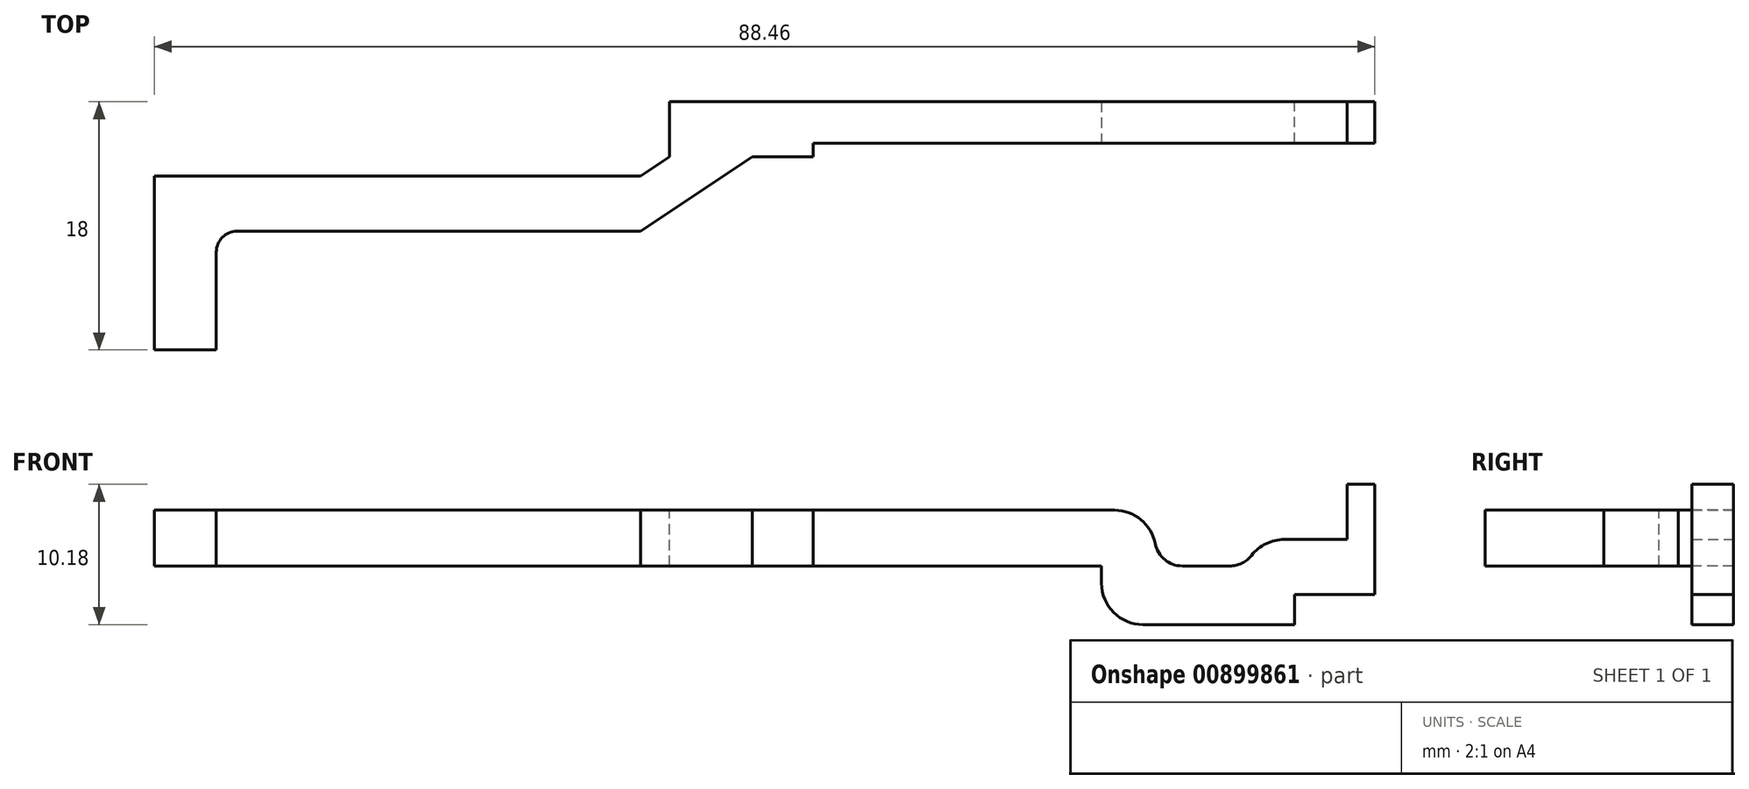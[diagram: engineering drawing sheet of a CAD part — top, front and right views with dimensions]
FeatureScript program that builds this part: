
annotation { "Feature Type Name" : "Feature", "Feature Type Description" : "" }
export const myFeature = defineFeature(function(context is Context, id is Id, definition is map)
    precondition{}
    {
        {
            var Q0;
            Q0=qCreatedBy(makeId("Top.planeOp"),FACE);
            var sketch = newSketch(context, id + "F0", { "sketchPlane" : qUnion([Q0])});
            skLineSegment(sketch, "E0.bottom", {"start": v(0, 0) * mm, "end": v(4.5, 0) * mm});
            skLineSegment(sketch, "E0.top", {"start": v(0, 8.6) * mm, "end": v(4.5, 8.6) * mm});
            skLineSegment(sketch, "E0.left", {"start": v(0, 0) * mm, "end": v(0, 8.6) * mm});
            skLineSegment(sketch, "E0.right", {"start": v(4.5, 0) * mm, "end": v(4.5, 8.6) * mm});
            skLineSegment(sketch, "E1.bottom", {"start": v(0, 8.6) * mm, "end": v(35.25, 8.6) * mm});
            skLineSegment(sketch, "E1.top", {"start": v(0, 12.6) * mm, "end": v(35.25, 12.6) * mm});
            skLineSegment(sketch, "E1.left", {"start": v(0, 8.6) * mm, "end": v(0, 12.6) * mm});
            skLineSegment(sketch, "E1.right", {"start": v(35.25, 8.6) * mm, "end": v(35.25, 12.6) * mm});
            skLineSegment(sketch, "E2.bottom", {"start": v(37.35, 18) * mm, "end": v(47.76, 18) * mm});
            skLineSegment(sketch, "E2.top", {"start": v(37.35, 14) * mm, "end": v(47.76, 14) * mm});
            skLineSegment(sketch, "E2.left", {"start": v(37.35, 18) * mm, "end": v(37.35, 14) * mm});
            skLineSegment(sketch, "E2.right", {"start": v(47.76, 18) * mm, "end": v(47.76, 14) * mm});
            skLineSegment(sketch, "E3", {"start": v(35.25, 12.6) * mm, "end": v(37.35, 14) * mm});
            skLineSegment(sketch, "E4", {"start": v(35.25, 8.6) * mm, "end": v(43.35, 14) * mm});
            skLineSegment(sketch, "E5.bottom", {"start": v(47.76, 18) * mm, "end": v(68.66, 18) * mm});
            skLineSegment(sketch, "E5.top", {"start": v(47.76, 15) * mm, "end": v(68.66, 15) * mm});
            skLineSegment(sketch, "E5.left", {"start": v(47.76, 18) * mm, "end": v(47.76, 15) * mm});
            skLineSegment(sketch, "E5.right", {"start": v(68.66, 18) * mm, "end": v(68.66, 15) * mm});
            skLineSegment(sketch, "E6.bottom", {"start": v(68.66, 18) * mm, "end": v(88.46, 18) * mm});
            skLineSegment(sketch, "E6.top", {"start": v(68.66, 15) * mm, "end": v(88.46, 15) * mm});
            skLineSegment(sketch, "E6.right", {"start": v(88.46, 18) * mm, "end": v(88.46, 15) * mm});
            skSolve(sketch);
        }
        {
            var Q0;
            Q0=makeQuery(id+"F0.imprint","IMPRINT",FACE,{"disambiguationData":[TD([[makeQuery(id+"F0.imprint","IMPRINT",EDGE,{"derivedFrom":sQuery(id+"F0.wireOp",EDGE,"E0.bottom")}),1.0]])]});
            var Q1;
            Q1=makeQuery(id+"F0.imprint","IMPRINT",FACE,{"disambiguationData":[TD([[makeQuery(id+"F0.imprint","IMPRINT",EDGE,{"derivedFrom":sQuery(id+"F0.wireOp",EDGE,"E1.top")}),-1.0]])]});
            var Q2;
            Q2=makeQuery(id+"F0.imprint","IMPRINT",FACE,{"disambiguationData":[TD([[makeQuery(id+"F0.imprint","IMPRINT",EDGE,{"derivedFrom":sQuery(id+"F0.wireOp",EDGE,"E1.right")}),-1.0]])]});
            var Q3;
            Q3=makeQuery(id+"F0.imprint","IMPRINT",FACE,{"disambiguationData":[TD([[makeQuery(id+"F0.imprint","IMPRINT",EDGE,{"derivedFrom":sQuery(id+"F0.wireOp",EDGE,"E2.bottom")}),-1.0]])]});
            var Q4;
            Q4=makeQuery(id+"F0.imprint","IMPRINT",FACE,{"disambiguationData":[TD([[makeQuery(id+"F0.imprint","IMPRINT",EDGE,{"derivedFrom":sQuery(id+"F0.wireOp",EDGE,"E5.bottom")}),-1.0]])]});
            extrude(context, id + "F1", {"entities" : qUnion([Q0, Q1, Q2, Q3, Q4]), "oppositeDirection" : true, "depth" : 4.05 * mm, "offsetDistance" : 25 * mm});
        }
        {
            var Q0;
            Q0=makeQuery(id+"F0.imprint","IMPRINT",FACE,{"disambiguationData":[TD([[makeQuery(id+"F0.imprint","IMPRINT",EDGE,{"derivedFrom":sQuery(id+"F0.wireOp",EDGE,"E6.bottom")}),-1.0]])]});
            extrude(context, id + "F2", {"entities" : qUnion([Q0]), "oppositeDirection" : true, "depth" : 8.3 * mm, "offsetDistance" : 25 * mm});
        }
        {
            var Q0;
            Q0=makeQuery(id+"F0.imprint","IMPRINT",FACE,{"disambiguationData":[TD([[makeQuery(id+"F0.imprint","IMPRINT",EDGE,{"derivedFrom":sQuery(id+"F0.wireOp",EDGE,"E6.bottom")}),-1.0]])]});
            extrude(context, id + "F3", {"entities" : qUnion([Q0]), "operationType" : NewBodyOperationType.ADD, "depth" : 1.88 * mm, "offsetDistance" : 25 * mm});
        }
        {
            var Q0;
            {var subQ0=sQuery(id+"F0.wireOp",EDGE,"E6.bottom");Q0=makeQuery(id+"F3.boolean.opBoolean","MERGE",FACE,{"derivedFrom":[makeQuery(id+"F2.opExtrude","SWEPT_FACE",FACE,{"disambiguationData":[OSD([subQ0])]}),makeQuery(id+"F3.opExtrude","SWEPT_FACE",FACE,{"disambiguationData":[OSD([subQ0])]})]});}
            var sketch = newSketch(context, id + "F4", { "sketchPlane" : qUnion([Q0])});
            skLineSegment(sketch, "E7.bottom", {"start": v(-86.46, 1.88) * mm, "end": v(-88.46, 1.88) * mm});
            skLineSegment(sketch, "E7.top", {"start": v(-86.46, -2.12) * mm, "end": v(-88.46, -2.12) * mm});
            skLineSegment(sketch, "E7.left", {"start": v(-86.46, 1.88) * mm, "end": v(-86.46, -2.12) * mm});
            skLineSegment(sketch, "E7.right", {"start": v(-88.46, 1.88) * mm, "end": v(-88.46, -2.12) * mm});
            skLineSegment(sketch, "E8.bottom", {"start": v(-88.46, -6.12) * mm, "end": v(-82.66, -6.12) * mm});
            skLineSegment(sketch, "E8.top", {"start": v(-88.46, -2.12) * mm, "end": v(-82.66, -2.12) * mm});
            skLineSegment(sketch, "E8.left", {"start": v(-88.46, -6.12) * mm, "end": v(-88.46, -2.12) * mm});
            skLineSegment(sketch, "E8.right", {"start": v(-82.66, -6.12) * mm, "end": v(-82.66, -2.12) * mm});
            skLineSegment(sketch, "E9", {"start": v(-68.66, -4.04) * mm, "end": v(-68.66, -8.3) * mm});
            skLineSegment(sketch, "E10", {"start": v(-88.46, -8.3) * mm, "end": v(-88.46, 1.88) * mm});
            skLineSegment(sketch, "E11", {"start": v(-68.66, 1.88) * mm, "end": v(-68.66, -4.04) * mm});
            skLineSegment(sketch, "E12", {"start": v(-82.66, -6.12) * mm, "end": v(-82.66, -8.3) * mm});
            skLineSegment(sketch, "E13", {"start": v(-82.66, -8.3) * mm, "end": v(-72.6, -8.3) * mm});
            skLineSegment(sketch, "E14", {"start": v(-72.6, -8.3) * mm, "end": v(-68.66, -8.3) * mm});
            skLineSegment(sketch, "E15", {"start": v(-68.66, 0) * mm, "end": v(-72.6, 0) * mm});
            skLineSegment(sketch, "E16", {"start": v(-72.6, 0) * mm, "end": v(-72.6, -4.04) * mm});
            skLineSegment(sketch, "E17", {"start": v(-72.6, -4.04) * mm, "end": v(-79.1, -4.04) * mm});
            skLineSegment(sketch, "E18", {"start": v(-79.1, -4.04) * mm, "end": v(-79.1, -2.12) * mm});
            skLineSegment(sketch, "E19", {"start": v(-79.1, -2.12) * mm, "end": v(-82.66, -2.12) * mm});
            skSolve(sketch);
        }
        {
            var Q0;
            {var subQ0=sQuery(id+"F4.wireOp",EDGE,"M4Aj1AxQ-FL5n-KYll-gw7S-FemKZirzfWIh");var subQ1=sQuery(id+"F4.wireOp",EDGE,"98212406-444c-4821-9b9e-8422945bcfc3");var subQ2=makeQuery(id+"F4.imprint","INTERSECT",VERTEX,{"disambiguationData":[OD(0.0)],"derivedFrom":[subQ1,subQ0]});Q0=makeQuery(id+"F4.imprint","IMPRINT",FACE,{"disambiguationData":[TD([[makeQuery(id+"F4.imprint","IMPRINT",EDGE,{"disambiguationData":[TD([[subQ2,-1.0]])],"derivedFrom":subQ1}),1.0]])]});}
            var Q1;
            {var subQ0=sQuery(id+"F4.wireOp",EDGE,"E8.bottom");Q1=makeQuery(id+"F4.imprint","IMPRINT",FACE,{"disambiguationData":[TD([[makeQuery(id+"F4.imprint","IMPRINT",EDGE,{"derivedFrom":subQ0}),-1.0]])]});}
            var Q2;
            {var subQ2=sQuery(id+"F4.wireOp",EDGE,"E7.left");Q2=makeQuery(id+"F4.imprint","IMPRINT",FACE,{"disambiguationData":[TD([[makeQuery(id+"F4.imprint","IMPRINT",EDGE,{"derivedFrom":subQ2}),1.0]])]});}
            extrude(context, id + "F5", {"entities" : qUnion([Q0, Q1, Q2]), "operationType" : NewBodyOperationType.REMOVE, "oppositeDirection" : true, "depth" : 25 * mm, "offsetDistance" : 25 * mm});
        }
        {
            var Q0;
            Q0=makeQuery(id+"F2.opExtrude","CAP_EDGE",EDGE,{"disambiguationData":[OSD([sQuery(id+"F0.wireOp",EDGE,"E5.right")])],"isStart":false});
            var Q1;
            Q1=makeQuery(id+"F5.boolean.opBoolean","COPY",EDGE,{"derivedFrom":makeQuery(id+"F5.opExtrude","SWEPT_EDGE",EDGE,{"disambiguationData":[OSD([sQuery(id+"F0.wireOp",EDGE,"E6.bottom"),sQuery(id+"F4.wireOp",EDGE,"E12"),sQuery(id+"F4.wireOp",EDGE,"E13")])]})});
            var Q2;
            Q2=makeQuery(id+"F5.boolean.opBoolean","COPY",EDGE,{"derivedFrom":makeQuery(id+"F5.opExtrude","SWEPT_EDGE",EDGE,{"disambiguationData":[OSD([sQuery(id+"F4.wireOp",EDGE,"E15"),sQuery(id+"F4.wireOp",EDGE,"E16")])]})});
            var Q3;
            Q3=makeQuery(id+"F5.boolean.opBoolean","COPY",EDGE,{"derivedFrom":makeQuery(id+"F5.opExtrude","SWEPT_EDGE",EDGE,{"disambiguationData":[OSD([sQuery(id+"F4.wireOp",EDGE,"E18"),sQuery(id+"F4.wireOp",EDGE,"E19")])]})});
            fillet(context, id + "F6", {"entities" : qUnion([Q0, Q1, Q2, Q3]), "radius" : 3 * mm, "tangentPropagation" : true, "allowEdgeOverflow" : false});
        }
        {
            var Q0;
            Q0=makeQuery(id+"F5.boolean.opBoolean","COPY",EDGE,{"derivedFrom":makeQuery(id+"F5.opExtrude","SWEPT_EDGE",EDGE,{"disambiguationData":[OSD([sQuery(id+"F4.wireOp",EDGE,"E16"),sQuery(id+"F4.wireOp",EDGE,"E17")])]})});
            var Q1;
            Q1=makeQuery(id+"F6.opFillet","BLEND_EDGE",EDGE,{"blendedFrom":[makeQuery(id+"F5.boolean.opBoolean","COPY",EDGE,{"derivedFrom":makeQuery(id+"F5.opExtrude","SWEPT_EDGE",EDGE,{"disambiguationData":[OSD([sQuery(id+"F4.wireOp",EDGE,"E18"),sQuery(id+"F4.wireOp",EDGE,"E19")])]})}),makeQuery(id+"F5.boolean.opBoolean","COPY",FACE,{"derivedFrom":makeQuery(id+"F5.opExtrude","SWEPT_FACE",FACE,{"disambiguationData":[OSD([sQuery(id+"F4.wireOp",EDGE,"E17")])]})})],"blendedInto":[makeQuery(id+"F5.boolean.opBoolean","COPY",FACE,{"derivedFrom":makeQuery(id+"F5.opExtrude","SWEPT_FACE",FACE,{"disambiguationData":[OSD([sQuery(id+"F4.wireOp",EDGE,"E17")])]})})]});
            fillet(context, id + "F7", {"entities" : qUnion([Q0, Q1]), "radius" : 2 * mm, "tangentPropagation" : true, "allowEdgeOverflow" : false});
        }
        {
            var Q0;
            Q0=makeQuery(id+"F1.opExtrude","SWEPT_EDGE",EDGE,{"disambiguationData":[OSD([sQuery(id+"F0.wireOp",EDGE,"E0.right"),sQuery(id+"F0.wireOp",EDGE,"E1.bottom")])]});
            fillet(context, id + "F8", {"entities" : qUnion([Q0]), "radius" : 1.5 * mm, "tangentPropagation" : true, "allowEdgeOverflow" : false});
        }
    });
